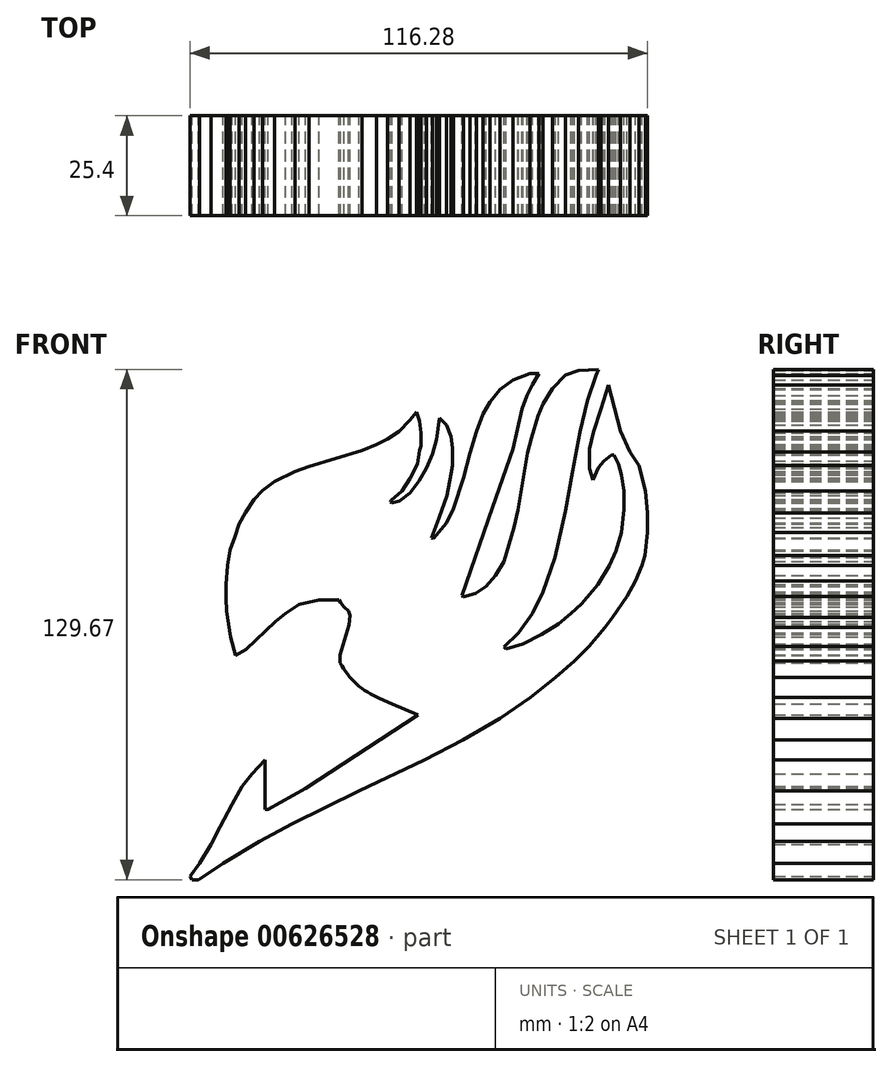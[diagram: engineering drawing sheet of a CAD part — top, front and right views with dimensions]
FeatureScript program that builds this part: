
annotation { "Feature Type Name" : "Feature", "Feature Type Description" : "" }
export const myFeature = defineFeature(function(context is Context, id is Id, definition is map)
    precondition{}
    {
        {
            var Q0;
            Q0=qCreatedBy(makeId("Front.planeOp"),FACE);
            var sketch = newSketch(context, id + "F0", { "sketchPlane" : qUnion([Q0])});
            skLineSegment(sketch, "E0", {"start": v(131.1, -39.27) * mm, "end": v(131.1, -26.7) * mm});
            skLineSegment(sketch, "E1", {"start": v(131.86, -39.27) * mm, "end": v(141.46, -33.93) * mm});
            skLineSegment(sketch, "E2", {"start": v(141.46, -33.93) * mm, "end": v(169.96, -15.32) * mm});
            skLineSegment(sketch, "E3", {"start": v(131.86, -39.27) * mm, "end": v(131.1, -39.27) * mm});
            skLineSegment(sketch, "E4", {"start": v(163.37, -12.44) * mm, "end": v(169.96, -15.32) * mm});
            skLineSegment(sketch, "E5", {"start": v(163.37, -12.44) * mm, "end": v(160.18, -11.1) * mm});
            skArc(sketch, "E6", {"start": v(150.2, -2.05) * mm, "mid": v(154.42, -7.43) * mm, "end": v(160.18, -11.1) * mm});
            skLineSegment(sketch, "E7", {"start": v(150.2, -2.05) * mm, "end": v(150.2, 0) * mm});
            skLineSegment(sketch, "E8", {"start": v(150.2, 0) * mm, "end": v(152.47, 7.54) * mm});
            skLineSegment(sketch, "E9", {"start": v(131.1, -26.7) * mm, "end": v(127.77, -30.27) * mm});
            skLineSegment(sketch, "E10", {"start": v(127.77, -30.27) * mm, "end": v(125.32, -33.38) * mm});
            skLineSegment(sketch, "E11", {"start": v(125.32, -33.38) * mm, "end": v(122.7, -37.95) * mm});
            skLineSegment(sketch, "E12", {"start": v(122.7, -37.95) * mm, "end": v(119.71, -43.77) * mm});
            skLineSegment(sketch, "E13", {"start": v(119.71, -43.77) * mm, "end": v(117.39, -48.2) * mm});
            skLineSegment(sketch, "E14", {"start": v(117.39, -48.2) * mm, "end": v(114.52, -52.98) * mm});
            skLineSegment(sketch, "E15", {"start": v(114.52, -52.98) * mm, "end": v(112.03, -56.3) * mm});
            skLineSegment(sketch, "E16", {"start": v(112.03, -56.3) * mm, "end": v(112.57, -57.14) * mm});
            skLineSegment(sketch, "E17", {"start": v(112.57, -57.14) * mm, "end": v(114.23, -57.14) * mm});
            skLineSegment(sketch, "E18", {"start": v(114.23, -57.14) * mm, "end": v(120.46, -52.94) * mm});
            skLineSegment(sketch, "E19", {"start": v(120.46, -52.94) * mm, "end": v(129.68, -47.38) * mm});
            skLineSegment(sketch, "E20", {"start": v(129.68, -47.38) * mm, "end": v(137.99, -43.02) * mm});
            skLineSegment(sketch, "E21", {"start": v(137.99, -43.02) * mm, "end": v(155.05, -34.59) * mm});
            skLineSegment(sketch, "E22", {"start": v(155.05, -34.59) * mm, "end": v(171.62, -26.7) * mm});
            skLineSegment(sketch, "E23", {"start": v(171.62, -26.7) * mm, "end": v(181.4, -21.58) * mm});
            skLineSegment(sketch, "E24", {"start": v(181.4, -21.58) * mm, "end": v(190.77, -16.15) * mm});
            skLineSegment(sketch, "E25", {"start": v(190.77, -16.15) * mm, "end": v(198.62, -10.8) * mm});
            skLineSegment(sketch, "E26", {"start": v(198.62, -10.8) * mm, "end": v(204.97, -5.81) * mm});
            skLineSegment(sketch, "E27", {"start": v(204.97, -5.81) * mm, "end": v(209.74, -1.57) * mm});
            skLineSegment(sketch, "E28", {"start": v(209.74, -1.57) * mm, "end": v(213.4, 2.16) * mm});
            skLineSegment(sketch, "E29", {"start": v(213.4, 2.16) * mm, "end": v(217.47, 6.98) * mm});
            skLineSegment(sketch, "E30", {"start": v(217.47, 6.98) * mm, "end": v(219.42, 9.43) * mm});
            skLineSegment(sketch, "E31", {"start": v(219.42, 9.43) * mm, "end": v(223.03, 14.79) * mm});
            skLineSegment(sketch, "E32", {"start": v(223.03, 14.79) * mm, "end": v(225.28, 18.82) * mm});
            skLineSegment(sketch, "E33", {"start": v(225.28, 18.82) * mm, "end": v(226.94, 22.64) * mm});
            skLineSegment(sketch, "E34", {"start": v(226.94, 22.64) * mm, "end": v(227.6, 25.25) * mm});
            skLineSegment(sketch, "E35", {"start": v(227.6, 25.25) * mm, "end": v(228.3, 31.02) * mm});
            skLineSegment(sketch, "E36", {"start": v(228.3, 31.02) * mm, "end": v(228.3, 36) * mm});
            skLineSegment(sketch, "E37", {"start": v(228.3, 36) * mm, "end": v(227.8, 41.61) * mm});
            skLineSegment(sketch, "E38", {"start": v(227.8, 41.61) * mm, "end": v(226.94, 44.9) * mm});
            skLineSegment(sketch, "E39", {"start": v(226.94, 44.9) * mm, "end": v(226.08, 48.13) * mm});
            skLineSegment(sketch, "E40", {"start": v(226.08, 48.13) * mm, "end": v(223.79, 51.46) * mm});
            skLineSegment(sketch, "E41", {"start": v(223.79, 51.46) * mm, "end": v(221.42, 56.91) * mm});
            skLineSegment(sketch, "E42", {"start": v(221.42, 56.91) * mm, "end": v(219.77, 63.1) * mm});
            skLineSegment(sketch, "E43", {"start": v(219.77, 63.1) * mm, "end": v(218.31, 68.6) * mm});
            skLineSegment(sketch, "E44", {"start": v(218.31, 68.6) * mm, "end": v(216.5, 62.5) * mm});
            skLineSegment(sketch, "E45", {"start": v(216.5, 62.5) * mm, "end": v(214.6, 56.57) * mm});
            skLineSegment(sketch, "E46", {"start": v(214.6, 56.57) * mm, "end": v(213.6, 52.26) * mm});
            skLineSegment(sketch, "E47", {"start": v(213.6, 52.26) * mm, "end": v(213.6, 47.28) * mm});
            skLineSegment(sketch, "E48", {"start": v(213.6, 47.28) * mm, "end": v(214.37, 44.38) * mm});
            skLineSegment(sketch, "E49", {"start": v(214.37, 44.38) * mm, "end": v(215.78, 47.6) * mm});
            skLineSegment(sketch, "E50", {"start": v(215.78, 47.6) * mm, "end": v(217.25, 49.27) * mm});
            skLineSegment(sketch, "E51", {"start": v(217.25, 49.27) * mm, "end": v(219.15, 50.74) * mm});
            skLineSegment(sketch, "E52", {"start": v(219.15, 50.74) * mm, "end": v(219.77, 50.74) * mm});
            skLineSegment(sketch, "E53", {"start": v(219.77, 50.74) * mm, "end": v(220.94, 48.52) * mm});
            skLineSegment(sketch, "E54", {"start": v(220.94, 48.52) * mm, "end": v(221.7, 45.65) * mm});
            skLineSegment(sketch, "E55", {"start": v(221.7, 45.65) * mm, "end": v(222.32, 41.61) * mm});
            skLineSegment(sketch, "E56", {"start": v(222.32, 41.61) * mm, "end": v(222.32, 40.41) * mm});
            skLineSegment(sketch, "E57", {"start": v(222.32, 40.41) * mm, "end": v(222.32, 36.86) * mm});
            skLineSegment(sketch, "E58", {"start": v(222.32, 36.86) * mm, "end": v(221.6, 31.02) * mm});
            skLineSegment(sketch, "E59", {"start": v(221.6, 31.02) * mm, "end": v(220.23, 26.39) * mm});
            skLineSegment(sketch, "E60", {"start": v(220.23, 26.39) * mm, "end": v(218.6, 22.64) * mm});
            skLineSegment(sketch, "E61", {"start": v(218.6, 22.64) * mm, "end": v(215.69, 17.9) * mm});
            skLineSegment(sketch, "E62", {"start": v(215.69, 17.9) * mm, "end": v(211.52, 12.88) * mm});
            skLineSegment(sketch, "E63", {"start": v(211.52, 12.88) * mm, "end": v(208.86, 10.56) * mm});
            skLineSegment(sketch, "E64", {"start": v(208.86, 10.56) * mm, "end": v(205.64, 7.86) * mm});
            skLineSegment(sketch, "E65", {"start": v(205.64, 7.86) * mm, "end": v(201.38, 5.16) * mm});
            skLineSegment(sketch, "E66", {"start": v(201.38, 5.16) * mm, "end": v(196.7, 2.7) * mm});
            skLineSegment(sketch, "E67", {"start": v(196.7, 2.7) * mm, "end": v(192.34, 1.54) * mm});
            skLineSegment(sketch, "E68", {"start": v(192.34, 1.54) * mm, "end": v(191.77, 2.01) * mm});
            skLineSegment(sketch, "E69", {"start": v(191.77, 2.01) * mm, "end": v(195.54, 5.55) * mm});
            skLineSegment(sketch, "E70", {"start": v(195.54, 5.55) * mm, "end": v(199.05, 10.56) * mm});
            skLineSegment(sketch, "E71", {"start": v(199.05, 10.56) * mm, "end": v(201.73, 16.02) * mm});
            skLineSegment(sketch, "E72", {"start": v(201.73, 16.02) * mm, "end": v(204.75, 24.67) * mm});
            skLineSegment(sketch, "E73", {"start": v(204.75, 24.67) * mm, "end": v(207.5, 36.5) * mm});
            skLineSegment(sketch, "E74", {"start": v(207.5, 36.5) * mm, "end": v(209.26, 46.45) * mm});
            skLineSegment(sketch, "E75", {"start": v(209.26, 46.45) * mm, "end": v(211.16, 56.57) * mm});
            skLineSegment(sketch, "E76", {"start": v(211.16, 56.57) * mm, "end": v(213.03, 64.57) * mm});
            skLineSegment(sketch, "E77", {"start": v(213.03, 64.57) * mm, "end": v(215.19, 70.98) * mm});
            skLineSegment(sketch, "E78", {"start": v(215.19, 70.98) * mm, "end": v(215.86, 72.53) * mm});
            skLineSegment(sketch, "E79", {"start": v(215.86, 72.53) * mm, "end": v(210.79, 72.25) * mm});
            skLineSegment(sketch, "E80", {"start": v(210.79, 72.25) * mm, "end": v(207.42, 71.1) * mm});
            skLineSegment(sketch, "E81", {"start": v(207.42, 71.1) * mm, "end": v(204.14, 67.67) * mm});
            skLineSegment(sketch, "E82", {"start": v(204.14, 67.67) * mm, "end": v(201.73, 63.7) * mm});
            skLineSegment(sketch, "E83", {"start": v(201.73, 63.7) * mm, "end": v(200.4, 60.66) * mm});
            skLineSegment(sketch, "E84", {"start": v(200.4, 60.66) * mm, "end": v(198.77, 55.13) * mm});
            skLineSegment(sketch, "E85", {"start": v(198.77, 55.13) * mm, "end": v(197.86, 51.22) * mm});
            skLineSegment(sketch, "E86", {"start": v(197.86, 51.22) * mm, "end": v(196.9, 45.53) * mm});
            skLineSegment(sketch, "E87", {"start": v(196.9, 45.53) * mm, "end": v(196.06, 40.6) * mm});
            skLineSegment(sketch, "E88", {"start": v(196.06, 40.6) * mm, "end": v(195.42, 36.77) * mm});
            skLineSegment(sketch, "E89", {"start": v(195.42, 36.77) * mm, "end": v(194.4, 32.37) * mm});
            skLineSegment(sketch, "E90", {"start": v(194.4, 32.37) * mm, "end": v(193.05, 27.83) * mm});
            skLineSegment(sketch, "E91", {"start": v(193.05, 27.83) * mm, "end": v(191.84, 23.74) * mm});
            skLineSegment(sketch, "E92", {"start": v(191.84, 23.74) * mm, "end": v(189.65, 20.15) * mm});
            skLineSegment(sketch, "E93", {"start": v(189.65, 20.15) * mm, "end": v(187.28, 17.3) * mm});
            skLineSegment(sketch, "E94", {"start": v(187.28, 17.3) * mm, "end": v(184.56, 15.53) * mm});
            skLineSegment(sketch, "E95", {"start": v(184.56, 15.53) * mm, "end": v(181.45, 14.7) * mm});
            skLineSegment(sketch, "E96", {"start": v(181.45, 14.7) * mm, "end": v(181.16, 15.02) * mm});
            skLineSegment(sketch, "E97", {"start": v(181.16, 15.02) * mm, "end": v(188.85, 37.38) * mm});
            skLineSegment(sketch, "E98", {"start": v(188.85, 37.38) * mm, "end": v(194.06, 52.26) * mm});
            skLineSegment(sketch, "E99", {"start": v(194.06, 52.26) * mm, "end": v(196, 60.6) * mm});
            skLineSegment(sketch, "E100", {"start": v(196, 60.6) * mm, "end": v(196.44, 62.43) * mm});
            skLineSegment(sketch, "E101", {"start": v(196.44, 62.43) * mm, "end": v(197.65, 65.9) * mm});
            skLineSegment(sketch, "E102", {"start": v(197.65, 65.9) * mm, "end": v(199.02, 68.69) * mm});
            skLineSegment(sketch, "E103", {"start": v(199.02, 68.69) * mm, "end": v(200.7, 71.46) * mm});
            skLineSegment(sketch, "E104", {"start": v(200.7, 71.46) * mm, "end": v(198.48, 71.46) * mm});
            skLineSegment(sketch, "E105", {"start": v(198.48, 71.46) * mm, "end": v(194.06, 69.8) * mm});
            skLineSegment(sketch, "E106", {"start": v(194.06, 69.8) * mm, "end": v(190.84, 67.38) * mm});
            skLineSegment(sketch, "E107", {"start": v(190.84, 67.38) * mm, "end": v(188.25, 64.27) * mm});
            skLineSegment(sketch, "E108", {"start": v(188.25, 64.27) * mm, "end": v(186.53, 61.13) * mm});
            skLineSegment(sketch, "E109", {"start": v(186.53, 61.13) * mm, "end": v(184.81, 56.7) * mm});
            skLineSegment(sketch, "E110", {"start": v(184.81, 56.7) * mm, "end": v(183.19, 51.22) * mm});
            skLineSegment(sketch, "E111", {"start": v(183.19, 51.22) * mm, "end": v(181.53, 44.9) * mm});
            skLineSegment(sketch, "E112", {"start": v(181.53, 44.9) * mm, "end": v(179.01, 37.14) * mm});
            skLineSegment(sketch, "E113", {"start": v(179.01, 37.14) * mm, "end": v(177.2, 33.42) * mm});
            skLineSegment(sketch, "E114", {"start": v(177.2, 33.42) * mm, "end": v(173.97, 29.54) * mm});
            skLineSegment(sketch, "E115", {"start": v(173.97, 29.54) * mm, "end": v(173.38, 29.64) * mm});
            skLineSegment(sketch, "E116", {"start": v(173.38, 29.64) * mm, "end": v(175.32, 34.8) * mm});
            skLineSegment(sketch, "E117", {"start": v(175.32, 34.8) * mm, "end": v(177.3, 40.43) * mm});
            skLineSegment(sketch, "E118", {"start": v(177.3, 40.43) * mm, "end": v(178.38, 45.92) * mm});
            skLineSegment(sketch, "E119", {"start": v(178.38, 45.92) * mm, "end": v(178.74, 48.06) * mm});
            skLineSegment(sketch, "E120", {"start": v(178.74, 48.06) * mm, "end": v(178.74, 52.58) * mm});
            skLineSegment(sketch, "E121", {"start": v(178.74, 52.58) * mm, "end": v(178.36, 55.44) * mm});
            skLineSegment(sketch, "E122", {"start": v(178.36, 55.44) * mm, "end": v(177.16, 58.33) * mm});
            skLineSegment(sketch, "E123", {"start": v(177.16, 58.33) * mm, "end": v(175.4, 60.2) * mm});
            skLineSegment(sketch, "E124", {"start": v(175.4, 60.2) * mm, "end": v(174.74, 54.7) * mm});
            skLineSegment(sketch, "E125", {"start": v(174.74, 54.7) * mm, "end": v(173.63, 50.96) * mm});
            skLineSegment(sketch, "E126", {"start": v(173.63, 50.96) * mm, "end": v(172.08, 47.4) * mm});
            skLineSegment(sketch, "E127", {"start": v(172.08, 47.4) * mm, "end": v(170.27, 44.1) * mm});
            skLineSegment(sketch, "E128", {"start": v(170.27, 44.1) * mm, "end": v(167.96, 41.1) * mm});
            skLineSegment(sketch, "E129", {"start": v(167.96, 41.1) * mm, "end": v(165.27, 39.09) * mm});
            skLineSegment(sketch, "E130", {"start": v(165.27, 39.09) * mm, "end": v(163.26, 38.55) * mm});
            skLineSegment(sketch, "E131", {"start": v(163.26, 38.55) * mm, "end": v(163.04, 38.83) * mm});
            skLineSegment(sketch, "E132", {"start": v(163.04, 38.83) * mm, "end": v(163.18, 39.15) * mm});
            skLineSegment(sketch, "E133", {"start": v(163.18, 39.15) * mm, "end": v(165.9, 41.61) * mm});
            skLineSegment(sketch, "E134", {"start": v(165.9, 41.61) * mm, "end": v(168, 44.76) * mm});
            skLineSegment(sketch, "E135", {"start": v(168, 44.76) * mm, "end": v(169.84, 48.52) * mm});
            skLineSegment(sketch, "E136", {"start": v(169.84, 48.52) * mm, "end": v(170.42, 51.94) * mm});
            skLineSegment(sketch, "E137", {"start": v(170.42, 51.94) * mm, "end": v(170.69, 53.1) * mm});
            skLineSegment(sketch, "E138", {"start": v(170.69, 53.1) * mm, "end": v(170.8, 56.34) * mm});
            skLineSegment(sketch, "E139", {"start": v(170.8, 56.34) * mm, "end": v(170.35, 59.4) * mm});
            skLineSegment(sketch, "E140", {"start": v(170.35, 59.4) * mm, "end": v(169.64, 61.73) * mm});
            skLineSegment(sketch, "E141", {"start": v(169.64, 61.73) * mm, "end": v(168, 59.6) * mm});
            skLineSegment(sketch, "E142", {"start": v(168, 59.6) * mm, "end": v(165.18, 56.67) * mm});
            skLineSegment(sketch, "E143", {"start": v(165.18, 56.67) * mm, "end": v(162.29, 54.8) * mm});
            skLineSegment(sketch, "E144", {"start": v(162.29, 54.8) * mm, "end": v(159.4, 53.37) * mm});
            skLineSegment(sketch, "E145", {"start": v(159.4, 53.37) * mm, "end": v(155.79, 51.95) * mm});
            skLineSegment(sketch, "E146", {"start": v(155.79, 51.95) * mm, "end": v(151.12, 50.53) * mm});
            skLineSegment(sketch, "E147", {"start": v(151.12, 50.53) * mm, "end": v(146.11, 49) * mm});
            skLineSegment(sketch, "E148", {"start": v(146.11, 49) * mm, "end": v(142.26, 47.84) * mm});
            skLineSegment(sketch, "E149", {"start": v(142.26, 47.84) * mm, "end": v(138.73, 46.59) * mm});
            skLineSegment(sketch, "E150", {"start": v(138.73, 46.59) * mm, "end": v(135.95, 45.21) * mm});
            skLineSegment(sketch, "E151", {"start": v(135.95, 45.21) * mm, "end": v(133.52, 44.01) * mm});
            skLineSegment(sketch, "E152", {"start": v(133.52, 44.01) * mm, "end": v(130.52, 41.76) * mm});
            skLineSegment(sketch, "E153", {"start": v(130.52, 41.76) * mm, "end": v(128.27, 39.41) * mm});
            skLineSegment(sketch, "E154", {"start": v(128.27, 39.41) * mm, "end": v(126.12, 36.13) * mm});
            skLineSegment(sketch, "E155", {"start": v(126.12, 36.13) * mm, "end": v(124.5, 33.19) * mm});
            skLineSegment(sketch, "E156", {"start": v(124.5, 33.19) * mm, "end": v(123.44, 30.1) * mm});
            skLineSegment(sketch, "E157", {"start": v(123.44, 30.1) * mm, "end": v(122.23, 26.65) * mm});
            skLineSegment(sketch, "E158", {"start": v(122.23, 26.65) * mm, "end": v(121.55, 22.64) * mm});
            skLineSegment(sketch, "E159", {"start": v(121.55, 22.64) * mm, "end": v(121.18, 17.82) * mm});
            skLineSegment(sketch, "E160", {"start": v(121.18, 17.82) * mm, "end": v(121.18, 14.34) * mm});
            skLineSegment(sketch, "E161", {"start": v(121.18, 14.34) * mm, "end": v(121.4, 11.1) * mm});
            skLineSegment(sketch, "E162", {"start": v(121.4, 11.1) * mm, "end": v(121.96, 7.37) * mm});
            skLineSegment(sketch, "E163", {"start": v(121.96, 7.37) * mm, "end": v(122.38, 4.58) * mm});
            skLineSegment(sketch, "E164", {"start": v(122.38, 4.58) * mm, "end": v(123.66, -0.22) * mm});
            skLineSegment(sketch, "E165", {"start": v(123.66, -0.22) * mm, "end": v(126.27, 1.37) * mm});
            skLineSegment(sketch, "E166", {"start": v(126.27, 1.37) * mm, "end": v(130.73, 5.55) * mm});
            skLineSegment(sketch, "E167", {"start": v(130.73, 5.55) * mm, "end": v(133.81, 8.43) * mm});
            skLineSegment(sketch, "E168", {"start": v(133.81, 8.43) * mm, "end": v(136.32, 10.56) * mm});
            skLineSegment(sketch, "E169", {"start": v(136.32, 10.56) * mm, "end": v(139.8, 12.73) * mm});
            skLineSegment(sketch, "E170", {"start": v(139.8, 12.73) * mm, "end": v(144.87, 13.97) * mm});
            skLineSegment(sketch, "E171", {"start": v(144.87, 13.97) * mm, "end": v(149.97, 13.97) * mm});
            skLineSegment(sketch, "E172", {"start": v(149.97, 13.97) * mm, "end": v(150.35, 13.23) * mm});
            skLineSegment(sketch, "E173", {"start": v(150.35, 13.23) * mm, "end": v(151.2, 12.1) * mm});
            skLineSegment(sketch, "E174", {"start": v(151.2, 12.1) * mm, "end": v(152.37, 11.13) * mm});
            skLineSegment(sketch, "E175", {"start": v(152.37, 11.13) * mm, "end": v(152.72, 9.98) * mm});
            skLineSegment(sketch, "E176", {"start": v(152.72, 9.98) * mm, "end": v(152.47, 7.54) * mm});
            skSolve(sketch);
        }
        {
            var Q0;
            Q0=makeQuery(id+"F0.imprint","IMPRINT",FACE,{"disambiguationData":[TD([[makeQuery(id+"F0.imprint","IMPRINT",EDGE,{"derivedFrom":sQuery(id+"F0.wireOp",EDGE,"E0")}),1.0]])]});
            extrude(context, id + "F1", {"entities" : qUnion([Q0]), "depth" : 25.4 * mm, "offsetDistance" : 25.4 * mm});
        }
    });
